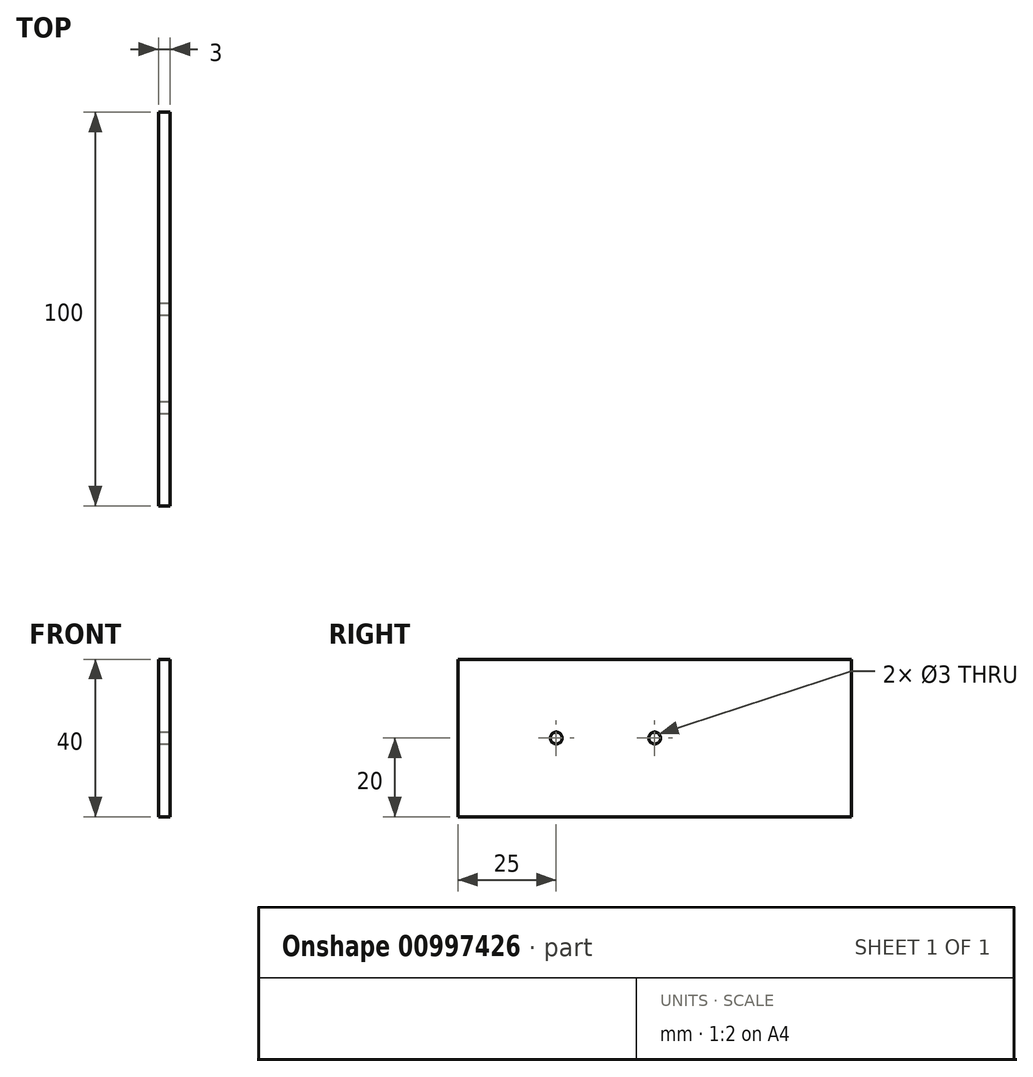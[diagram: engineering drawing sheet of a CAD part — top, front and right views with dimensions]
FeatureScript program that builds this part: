
annotation { "Feature Type Name" : "Feature", "Feature Type Description" : "" }
export const myFeature = defineFeature(function(context is Context, id is Id, definition is map)
    precondition{}
    {
        {
            var Q0;
            Q0=qCreatedBy(makeId("Right.planeOp"),FACE);
            var sketch = newSketch(context, id + "F0", { "sketchPlane" : qUnion([Q0])});
            skLineSegment(sketch, "E0.bottom", {"start": v(0, 0) * mm, "end": v(100, 0) * mm});
            skLineSegment(sketch, "E0.top", {"start": v(0, -40) * mm, "end": v(100, -40) * mm});
            skLineSegment(sketch, "E0.left", {"start": v(0, 0) * mm, "end": v(0, -40) * mm});
            skLineSegment(sketch, "E0.right", {"start": v(100, 0) * mm, "end": v(100, -40) * mm});
            skSolve(sketch);
        }
        {
            var Q0;
            Q0=makeQuery(id+"F0.imprint","IMPRINT",FACE,{"disambiguationData":[TD([[makeQuery(id+"F0.imprint","IMPRINT",EDGE,{"derivedFrom":sQuery(id+"F0.wireOp",EDGE,"E0.bottom")}),-1.0]])]});
            extrude(context, id + "F1", {"entities" : qUnion([Q0]), "oppositeDirection" : true, "depth" : 3 * mm, "offsetDistance" : 25 * mm});
        }
        {
            var Q0;
            Q0=makeQuery(id+"F1.opExtrude","CAP_FACE",FACE,{"disambiguationData":[OSD([sQuery(id+"F0.wireOp",EDGE,"E0.bottom"),sQuery(id+"F0.wireOp",EDGE,"E0.top"),sQuery(id+"F0.wireOp",EDGE,"E0.left"),sQuery(id+"F0.wireOp",EDGE,"E0.right")])],"isStart":true});
            var sketch = newSketch(context, id + "F2", { "sketchPlane" : qUnion([Q0])});
            skLineSegment(sketch, "E1", {"start": v(25, -20) * mm, "end": v(50, -20) * mm});
            skSolve(sketch);
        }
        {
            var Q0;
            Q0=sQuery(id+"F2.wireOp",VERTEX,"E1.end");
            var Q1;
            Q1=sQuery(id+"F2.wireOp",VERTEX,"E1.start");
            var Q2;
            Q2=makeQuery(id+"F1.opExtrude","SWEPT_BODY",BODY,{"disambiguationData":[OSD([sQuery(id+"F0.wireOp",EDGE,"E0.bottom"),sQuery(id+"F0.wireOp",EDGE,"E0.top"),sQuery(id+"F0.wireOp",EDGE,"E0.left"),sQuery(id+"F0.wireOp",EDGE,"E0.right")])]});
            hole(context, id + "F3", {"style" : HoleStyle.SIMPLE, "endStyle" : HoleEndStyle.THROUGH, "holeDiameter" : 3 * mm, "majorDiameter" : 5 * mm, "isTappedThrough" : true, "tappedDepth" : 12 * mm, "tapClearance" : 3, "locations" : qUnion([Q0, Q1]), "scope" : qUnion([Q2])});
        }
    });
